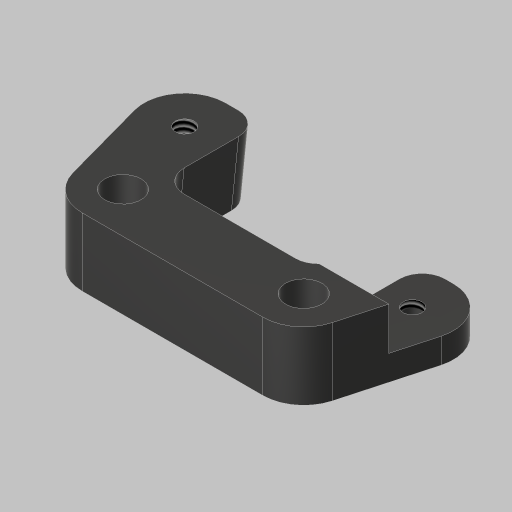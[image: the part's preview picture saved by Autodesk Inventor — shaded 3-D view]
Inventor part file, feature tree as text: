
AUTODESK INVENTOR PART (.ipt)
format: ipt  version: 2023.5 (Build 275446000, 446)  size: 274,432 bytes
history: native  units: in
note: dims shown in document units (in); Inventor stores cm internally (conversion verified against a paired STEP export)
features: sketch x5, extrude x4, hole x2, fillet x2, projected_geometry x1
ambient origin geometry x8: Origin, YZ Plane, XZ Plane, XY Plane, X Axis, Y Axis, Z Axis, Center Point
bodies: Solid1 (feature_tree)
feature tree (14):
  sketch  "Sketch1"  dims[d0=1.13in d1=1.0in]
  sketch  "Sketch2"  dims[d2=1.375in d3=1.75in]
  extrude  "Extrusion1"  Depth=1.0in
  hole  "Hole1"  [1 undecoded]
  hole  "Hole2"  [1 undecoded]
  sketch  "Sketch3"  dims[d4=2.5in d5=2.3622in d7=360.0deg]
  extrude  "Extrusion3"  Depth=0.375in
  fillet  "Fillet2"  Radius=1.2773in
  extrude  "Extrusion4"  Depth=0.5118in
  extrude  "Extrusion2"  Depth=0.5118in
  fillet  "Fillet1"  Radius=4.2441in
  sketch  "Sketch4"  dims[d9=0.375in d10=1.2773in d11=1.2773in]
  sketch  "Sketch5"  dims[d12=0.201in d14=0.0237in d15=1.2598in d16=4.2441in d18=1.6in d19=0.201in d20=0.275in d21=0.201in d22=0.201in d23=0.125in d24=0.375in d25=0.0in d26=0.201in d27=0.38in d28=0.385in d29=0.25in d30=0.5635in d31=1.0in d32=0.8108in d33=0.104in d34=0.276in d35=0.375in d36=0.25in d37=0.5635in d38=1.0in d39=0.8108in d40=0.9449in d41=0.6106in d42=0.0in d43=0.0in d44=0.125in d45=0.8661in d46=0.8661in d47=0.9449in d48=0.5512in d49=0.0in d50=0.125in d53=1.0in d54=0.0in d55=0.2362in d56=0.5118in]
  projected_geometry  "Project Cut Edges1"
note: 2 required parameter values undecoded (feature->parameter linkage not recoverable at this tier; creation-order binding heuristic only, values carry confidence <= 0.55)
